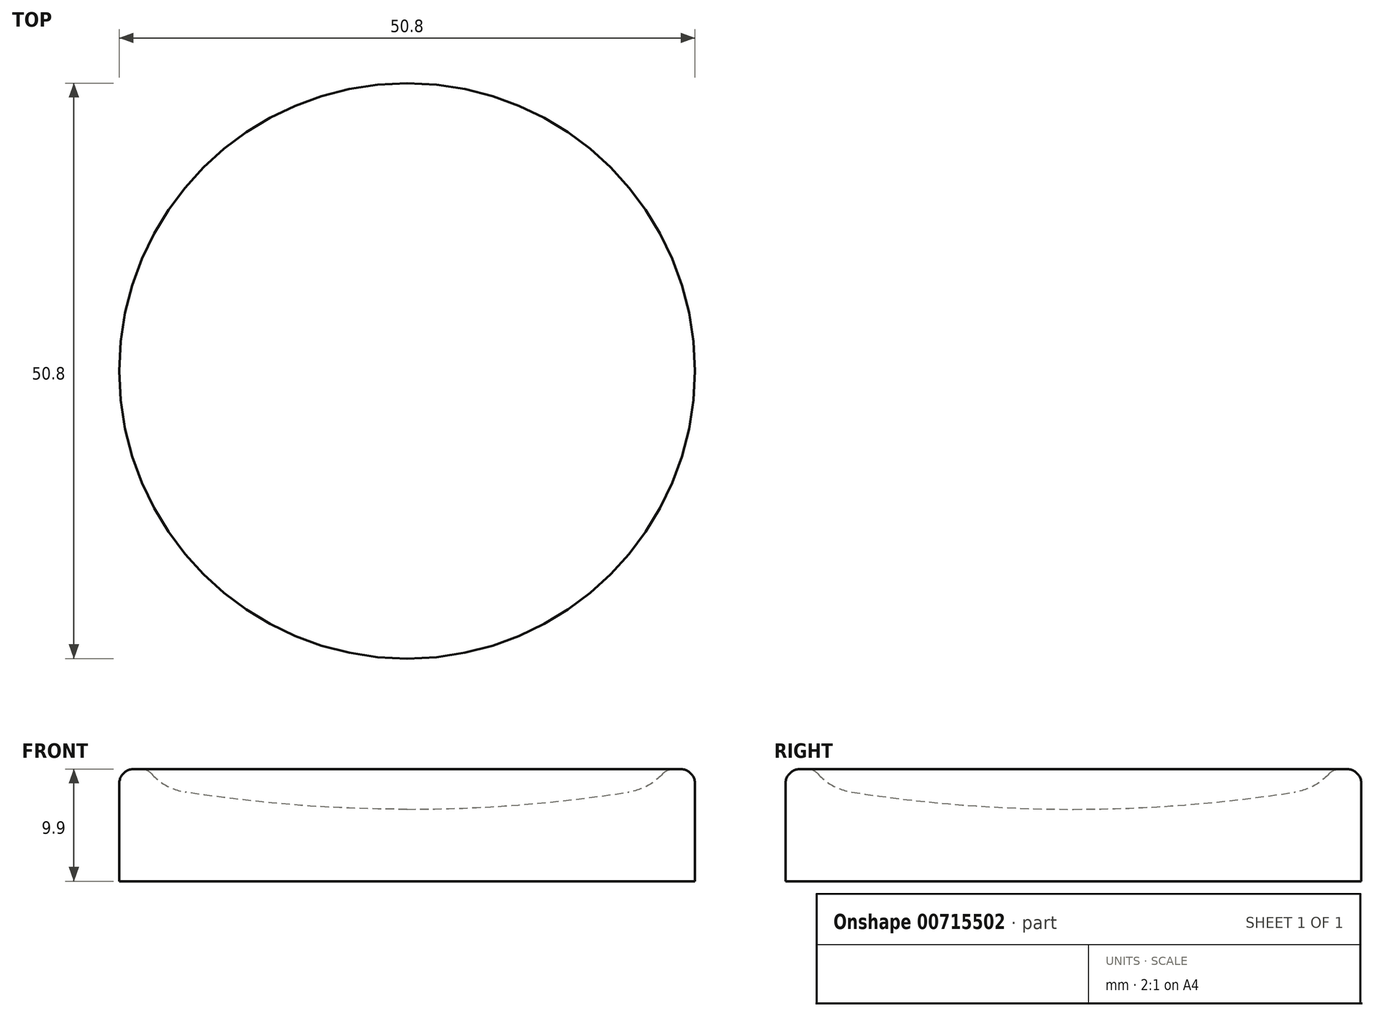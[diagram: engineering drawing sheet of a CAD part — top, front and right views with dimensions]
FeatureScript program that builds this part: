
annotation { "Feature Type Name" : "Feature", "Feature Type Description" : "" }
export const myFeature = defineFeature(function(context is Context, id is Id, definition is map)
    precondition{}
    {
        {
            var Q0;
            Q0=qCreatedBy(makeId("Front.planeOp"),FACE);
            var sketch = newSketch(context, id + "F0", { "sketchPlane" : qUnion([Q0])});
            skArc(sketch, "E0", {"start": v(0, 6.35) * mm, "mid": v(-11.16, 6.84) * mm, "end": v(-22.23, 8.3) * mm});
            skLineSegment(sketch, "E1", {"start": v(0, 6.35) * mm, "end": v(0, 0) * mm});
            skLineSegment(sketch, "E2", {"start": v(-25.4, 9.9) * mm, "end": v(-25.4, 0) * mm});
            skLineSegment(sketch, "E3", {"start": v(0, 0) * mm, "end": v(-25.4, 0) * mm});
            skLineSegment(sketch, "E4", {"start": v(-25.4, 9.9) * mm, "end": v(-22.23, 9.9) * mm});
            skLineSegment(sketch, "E5", {"start": v(-22.23, 8.3) * mm, "end": v(-22.23, 9.9) * mm});
            skSolve(sketch);
        }
        {
            var Q0;
            Q0 = qSketchRegion(id + "F0", true);
            var Q1;
            Q1=sQuery(id+"F0.wireOp",EDGE,"E1");
            revolve(context, id + "F1", {"surfaceOperationType" : NewSurfaceOperationType.NEW, "entities" : qUnion([Q0]), "axis" : qUnion([Q1]), "revolveType" : RevolveType.FULL});
        }
        {
            var Q0;
            Q0=makeQuery(id+"F1.opRevolve","SWEPT_EDGE",EDGE,{"disambiguationData":[OSD([sQuery(id+"F0.wireOp",EDGE,"E4"),sQuery(id+"F0.wireOp",EDGE,"E5")])]});
            var Q1;
            Q1=makeQuery(id+"F1.opRevolve","SWEPT_EDGE",EDGE,{"disambiguationData":[OSD([sQuery(id+"F0.wireOp",EDGE,"E2"),sQuery(id+"F0.wireOp",EDGE,"E4")])]});
            fillet(context, id + "F2", {"entities" : qUnion([Q0, Q1]), "radius" : 1.27 * mm, "tangentPropagation" : true, "allowEdgeOverflow" : false});
        }
        {
            var Q0;
            Q0=makeQuery(id+"F1.opRevolve","SWEPT_EDGE",EDGE,{"disambiguationData":[OSD([sQuery(id+"F0.wireOp",EDGE,"E0"),sQuery(id+"F0.wireOp",EDGE,"E5")])]});
            fillet(context, id + "F3", {"entities" : qUnion([Q0]), "radius" : 5.08 * mm, "tangentPropagation" : true, "allowEdgeOverflow" : false});
        }
    });
